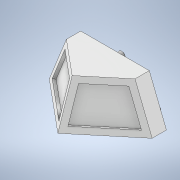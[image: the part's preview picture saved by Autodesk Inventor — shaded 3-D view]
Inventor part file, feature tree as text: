
AUTODESK INVENTOR PART (.ipt)
format: ipt  version: 2020 (Build 240168000, 168)  size: 167,424 bytes
history: native  units: in
note: dims shown in document units (in); Inventor stores cm internally (conversion verified against a paired STEP export)
features: sketch x5, extrude x3, plane x1, loft x1, shell x1, chamfer x1
ambient origin geometry x8: Origin, YZ Plane, XZ Plane, XY Plane, X Axis, Y Axis, Z Axis, Center Point
bodies: Solid1 (feature_tree)
feature tree (12):
  sketch  "Sketch1"  dims[d0=1.8in d1=0.25in d2=0.25in]
  plane  "Work Plane1"
  loft  "Loft1"
  shell  "Shell1"  Thickness=0.25in
  extrude  "Extrusion1"  Depth=0.9in
  extrude  "Extrusion2"  Depth=0.25in
  extrude  "Extrusion3"  Depth=0.25in
  chamfer  "Chamfer1"  Distance=0.75in
  sketch  "Sketch2"  dims[d3=1.0in d4=0.9in]
  sketch  "Sketch6"  dims[d5=0.75in d6=0.25in]
  sketch  "Sketch7"  dims[d7=0.25in d9=0.3in]
  sketch  "Sketch8"  dims[d10=0.3in d11=0.75in d12=0.6in d13=0.0in d14=90.0deg d15=0.0in d16=90.0deg d17=0.1in d18=0.1in d19=0.05in d20=0.0in d21=0.1in d22=0.05in d23=0.0in d24=0.1247in d25=0.125in d26=0.125in d27=1.25in d28=0.275in d29=0.625in d30=0.9in d31=0.125in d32=0.125in d33=0.125in d34=0.0in d35=0.01in d36=0.125in d37=45.0deg]
